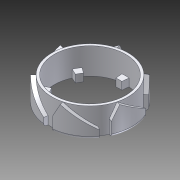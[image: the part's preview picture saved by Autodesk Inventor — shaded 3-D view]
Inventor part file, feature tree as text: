
AUTODESK INVENTOR PART (.ipt)
format: ipt  version: 2012 (Build 160160000, 160)  size: 314,368 bytes
history: native  units: mm
features: extrude x9, sketch x7, pattern_circular x6, helix x6, mirror x4, fillet x2, chamfer x1
ambient origin geometry x8: Origin, YZ Plane, XZ Plane, XY Plane, X Axis, Y Axis, Z Axis, Center Point
bodies: Solid1 (feature_tree)
feature tree (35):
  sketch  "Sketch1"  dims[d0=64.0mm d1=54.2mm]
  extrude  "Extrusion1"  Depth=54.2mm
  extrude  "Extrusion2"  Depth=58.0mm
  extrude  "Extrusion3"  Depth=20.0mm TaperAngle=0.0deg
  extrude  "Extrusion4"  Depth=4.0mm
  mirror  "Mirror1"
  fillet  "Fillet2"  Radius=4.0mm
  extrude  "Extrusion5"  Depth=16.0mm
  mirror  "Mirror2"
  pattern_circular  "Circular Pattern3"  Count=6 Angle=360.0deg
  sketch  "Sketch3"  dims[d4=1.0mm d5=0.0mm d6=20.0mm d7=0.0mm]
  extrude  "Extrusion6"  Depth=30.0mm TaperAngle=360.0deg
  mirror  "Mirror3"
  pattern_circular  "Circular Pattern4"  [2 undecoded]
  extrude  "Extrusion7"  Depth=1.012291mm
  mirror  "Mirror4"
  pattern_circular  "Circular Pattern5"  [2 undecoded]
  chamfer  "Chamfer1"  Distance=60.0mm Angle=360.0deg
  pattern_circular  "Circular Pattern2"  [2 undecoded]
  fillet  "Fillet3"  Radius=5.8mm
  helix  "Coil1"  [1 undecoded]
  extrude  "Extrusion8"  Depth=16.0mm TaperAngle=45.0deg
  sketch  "Sketch5"  dims[d17=2.0mm d18=16.0mm d19=60.0mm d20=360.0deg]
  helix  "Coil2"  [1 undecoded]
  helix  "Coil3"  [1 undecoded]
  helix  "Coil4"  [1 undecoded]
  extrude  "Extrusion9"  Depth=4.0mm
  pattern_circular  "Circular Pattern6"  [2 undecoded]
  sketch  "Sketch7"  dims[d27=44.1mm d28=55.0mm d29=1.012291mm d30=5.8mm d31=0.0mm d32=60.0mm d33=360.0deg d35=40.1mm d36=49.0mm d37=1.012291mm d38=5.8mm d39=0.0mm d40=60.0mm d41=360.0deg d43=16.0mm d44=17.0mm d45=45.0deg d46=2.0mm d47=4.0mm d48=20.0mm d49=16.0mm d50=1.666667mm d51=0.0mm d52=90.0deg d53=90.0deg d54=0.0mm d55=0.0mm d56=10.0mm d57=0.0mm d58=4.0mm d59=26.0mm d60=20.0mm d61=18.0mm d62=1.25mm d63=0.0mm d64=90.0deg d65=90.0deg d66=0.0mm d67=0.0mm d68=20.0mm d69=20.0mm d70=1.666667mm d71=0.0mm d72=90.0deg d73=90.0deg d74=0.0mm d75=0.0mm d76=4.0mm d77=20.0mm d78=18.0mm d79=0.416667mm d80=0.0mm d81=90.0deg d82=90.0deg d83=0.0mm d84=0.0mm d86=2.094395mm d87=10.0mm d88=0.0mm d89=60.0mm d90=360.0deg d92=1.047198mm d93=29.0mm d94=22.0mm d95=10.0mm d96=16.0mm d97=1.25mm d98=0.0mm d99=90.0deg d100=90.0deg d101=0.0mm d102=0.0mm d103=16.0mm d104=10.0mm d105=16.0mm d106=0.416667mm d107=0.0mm d108=90.0deg d109=90.0deg d110=0.0mm d111=0.0mm d112=60.0mm d113=360.0deg d115=18.0mm]
  helix  "Coil5"  [1 undecoded]
  helix  "Coil6"  [1 undecoded]
  pattern_circular  "Circular Pattern7"  [2 undecoded]
  sketch  "Sketch2"  dims[d2=50.0mm d3=58.0mm]
  sketch  "Sketch4"  dims[d8=4.0mm d9=0.0mm d10=4.0mm d11=4.0mm d12=0.0mm]
  sketch  "Sketch6"  dims[d22=3.0mm d23=0.0mm d24=30.0mm d25=360.0deg]
note: 16 required parameter values undecoded (feature->parameter linkage not recoverable at this tier; creation-order binding heuristic only, values carry confidence <= 0.55)
